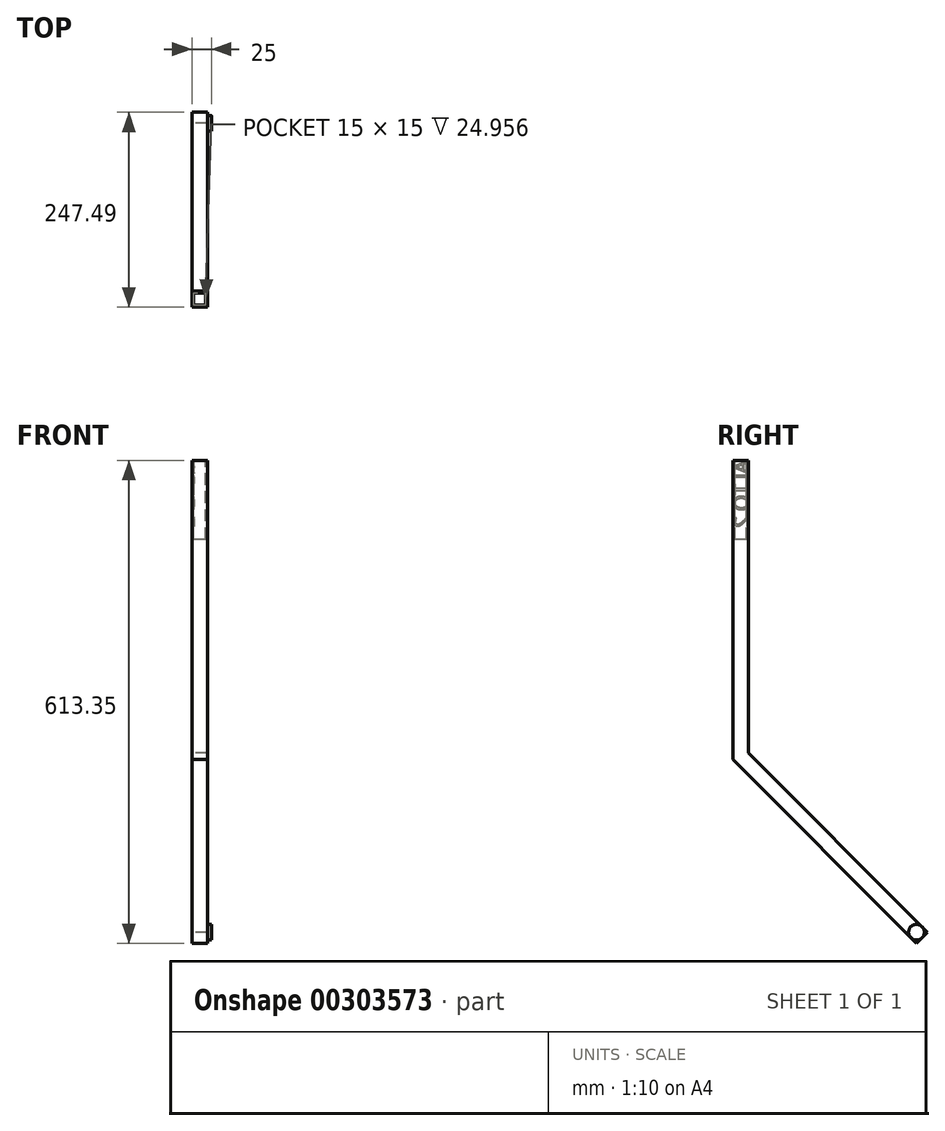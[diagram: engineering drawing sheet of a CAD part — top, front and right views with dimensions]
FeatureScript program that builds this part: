
annotation { "Feature Type Name" : "Feature", "Feature Type Description" : "" }
export const myFeature = defineFeature(function(context is Context, id is Id, definition is map)
    precondition{}
    {
        {
            var Q0;
            Q0=qCreatedBy(makeId("Right.planeOp"),FACE);
            var sketch = newSketch(context, id + "F0", { "sketchPlane" : qUnion([Q0])});
            skLineSegment(sketch, "E0.bottom", {"start": v(-73.87, 203.36) * mm, "end": v(-53.87, 203.36) * mm});
            skLineSegment(sketch, "E0.left", {"start": v(-73.87, 203.36) * mm, "end": v(-73.87, -176.64) * mm});
            skLineSegment(sketch, "E0.right", {"start": v(-53.87, 203.36) * mm, "end": v(-53.87, -168.36) * mm});
            skLineSegment(sketch, "E1", {"start": v(-53.87, -168.36) * mm, "end": v(173.62, -395.85) * mm});
            skLineSegment(sketch, "E2", {"start": v(173.62, -395.85) * mm, "end": v(159.48, -409.99) * mm});
            skLineSegment(sketch, "E3", {"start": v(159.48, -409.99) * mm, "end": v(-73.87, -176.64) * mm});
            skLineSegment(sketch, "E4", {"start": v(-147.1, -386.46) * mm, "end": v(66.8, -600.37) * mm, "construction": true});
            skLineSegment(sketch, "E5", {"start": v(-73.87, -176.64) * mm, "end": v(-53.87, -168.36) * mm});
            skSolve(sketch);
        }
        {
            var Q0;
            Q0=makeQuery(id+"F0.imprint","IMPRINT",FACE,{"disambiguationData":[TD([[makeQuery(id+"F0.imprint","IMPRINT",EDGE,{"derivedFrom":sQuery(id+"F0.wireOp",EDGE,"E0.bottom")}),-1.0]])]});
            var Q1;
            Q1=makeQuery(id+"F0.imprint","IMPRINT",FACE,{"disambiguationData":[TD([[makeQuery(id+"F0.imprint","IMPRINT",EDGE,{"derivedFrom":sQuery(id+"F0.wireOp",EDGE,"E1")}),-1.0]])]});
            extrude(context, id + "F1", {"entities" : qUnion([Q0, Q1]), "depth" : 20 * mm});
        }
        {
            var Q0;
            Q0=makeQuery(id+"F1.opExtrude","CAP_FACE",FACE,{"disambiguationData":[OSD([sQuery(id+"F0.wireOp",EDGE,"E0.bottom"),sQuery(id+"F0.wireOp",EDGE,"E0.left"),sQuery(id+"F0.wireOp",EDGE,"E0.right"),sQuery(id+"F0.wireOp",EDGE,"E1"),sQuery(id+"F0.wireOp",EDGE,"E2"),sQuery(id+"F0.wireOp",EDGE,"E3")])],"isStart":false});
            var sketch = newSketch(context, id + "F2", { "sketchPlane" : qUnion([Q0])});
            skLineSegment(sketch, "E6", {"start": v(159.48, -409.99) * mm, "end": v(159.48, -358.98) * mm, "construction": true});
            skLineSegment(sketch, "E7", {"start": v(173.62, -395.85) * mm, "end": v(101.05, -395.85) * mm, "construction": true});
            skCircle(sketch, "E8", {"center": v(159.48, -395.85) * mm, "radius": 10 * mm});
            skSolve(sketch);
        }
        {
            var Q0;
            {var subQ0=sQuery(id+"F2.wireOp",EDGE,"E8");var subQ1=makeQuery(id+"F2.imprint","INTERSECT",VERTEX,{"derivedFrom":[makeQuery(id+"F1.opExtrude","CAP_EDGE",EDGE,{"disambiguationData":[OSD([sQuery(id+"F0.wireOp",EDGE,"E3")])],"isStart":false}),subQ0]});Q0=makeQuery(id+"F2.imprint","IMPRINT",FACE,{"disambiguationData":[TD([[makeQuery(id+"F2.imprint","IMPRINT",EDGE,{"disambiguationData":[TD([[subQ1,1.0]])],"derivedFrom":subQ0}),1.0]])]});}
            extrude(context, id + "F3", {"entities" : qUnion([Q0]), "operationType" : NewBodyOperationType.ADD, "depth" : 5 * mm});
        }
        {
            var Q0;
            Q0=makeQuery(id+"F1.opExtrude","CAP_FACE",FACE,{"disambiguationData":[OSD([sQuery(id+"F0.wireOp",EDGE,"E0.bottom"),sQuery(id+"F0.wireOp",EDGE,"E0.left"),sQuery(id+"F0.wireOp",EDGE,"E0.right"),sQuery(id+"F0.wireOp",EDGE,"E1"),sQuery(id+"F0.wireOp",EDGE,"E2"),sQuery(id+"F0.wireOp",EDGE,"E3")])],"isStart":true});
            var sketch = newSketch(context, id + "F4", { "sketchPlane" : qUnion([Q0])});
            skLineSegment(sketch, "E9.bottom", {"start": v(73.87, -176.64) * mm, "end": v(53.87, -176.64) * mm, "construction": true});
            skLineSegment(sketch, "E9.top", {"start": v(73.87, -156.64) * mm, "end": v(53.87, -156.64) * mm, "construction": true});
            skLineSegment(sketch, "E9.left", {"start": v(73.87, -176.64) * mm, "end": v(73.87, -156.64) * mm, "construction": true});
            skLineSegment(sketch, "E9.right", {"start": v(53.87, -176.64) * mm, "end": v(53.87, -156.64) * mm, "construction": true});
            skPoint(sketch, "E9.middle", {"position": v(63.87, -166.64) * mm});
            skSolve(sketch);
        }
        {
            var Q0;
            Q0=makeQuery(id+"F1.opExtrude","SWEPT_FACE",FACE,{"disambiguationData":[OSD([sQuery(id+"F0.wireOp",EDGE,"E0.bottom")])]});
            var sketch = newSketch(context, id + "F5", { "sketchPlane" : qUnion([Q0])});
            skLineSegment(sketch, "E10.bottom", {"start": v(17.5, -56.37) * mm, "end": v(2.5, -56.37) * mm});
            skLineSegment(sketch, "E10.top", {"start": v(17.5, -71.37) * mm, "end": v(2.5, -71.37) * mm});
            skLineSegment(sketch, "E10.left", {"start": v(17.5, -56.37) * mm, "end": v(17.5, -71.37) * mm});
            skLineSegment(sketch, "E10.right", {"start": v(2.5, -56.37) * mm, "end": v(2.5, -71.37) * mm});
            skPoint(sketch, "E10.middle", {"position": v(10, -63.87) * mm});
            skPoint(sketch, "E10.middle.positionSnap0", {"position": v(20, -63.87) * mm});
            skPoint(sketch, "E10.middle.positionSnap1", {"position": v(10, -73.87) * mm});
            skPoint(sketch, "E10.centerSnap0", {"position": v(20, -63.87) * mm});
            skPoint(sketch, "E10.centerSnap1", {"position": v(10, -73.87) * mm});
            skSolve(sketch);
        }
        {
            var Q0;
            Q0=makeQuery(id+"F5.imprint","IMPRINT",FACE,{"disambiguationData":[TD([[makeQuery(id+"F5.imprint","IMPRINT",EDGE,{"derivedFrom":sQuery(id+"F5.wireOp",EDGE,"E10.bottom")}),1.0]])]});
            extrude(context, id + "F6", {"entities" : qUnion([Q0]), "operationType" : NewBodyOperationType.REMOVE, "oppositeDirection" : true, "depth" : 100 * mm});
        }
        {
            var Q0;
            Q0=makeQuery(id+"F4.imprint","IMPRINT",FACE,{"disambiguationData":[TD([[makeQuery(id+"F4.imprint","IMPRINT",EDGE,{"derivedFrom":makeQuery(id+"F1.opExtrude","CAP_EDGE",EDGE,{"disambiguationData":[OSD([sQuery(id+"F0.wireOp",EDGE,"E0.bottom")])],"isStart":true})}),1.0]])]});
            var sketch = newSketch(context, id + "F7", { "sketchPlane" : qUnion([Q0])});
            skText(sketch, "E11", { "text": "ALTO 2\n", "fontName": "OpenSans-Regular.ttf"});
            const initialGuessF7  = {"E11": [0.05387, 0.20336, 0, -1, 0.01855]};
            skSetInitialGuess(sketch, initialGuessF7);
            skSolve(sketch);
        }
        {
            var Q0;
            Q0 = qSketchRegion(id + "F7", true);
            extrude(context, id + "F8", {"entities" : qUnion([Q0]), "operationType" : NewBodyOperationType.REMOVE, "oppositeDirection" : true, "depth" : 3 * mm});
        }
    });
